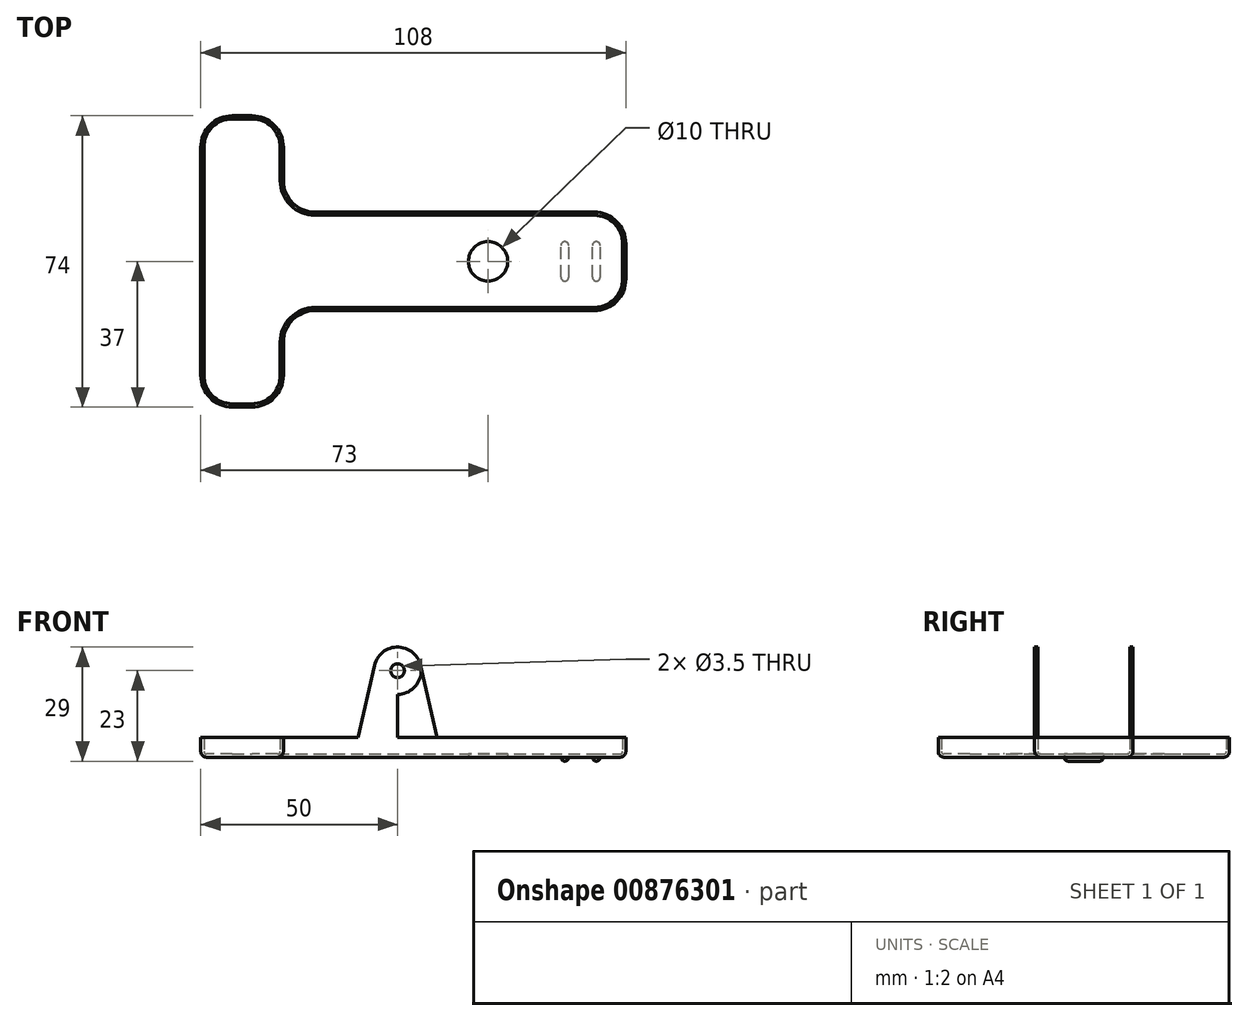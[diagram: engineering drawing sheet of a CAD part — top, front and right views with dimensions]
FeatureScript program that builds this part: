
annotation { "Feature Type Name" : "Feature", "Feature Type Description" : "" }
export const myFeature = defineFeature(function(context is Context, id is Id, definition is map)
    precondition{}
    {
        {
            var Q0;
            Q0=qCreatedBy(makeId("Top.planeOp"),FACE);
            var sketch = newSketch(context, id + "F0", { "sketchPlane" : qUnion([Q0])});
            skLineSegment(sketch, "E0.bottom", {"start": v(54, 12.5) * mm, "end": v(-54, 12.5) * mm});
            skLineSegment(sketch, "E0.top", {"start": v(54, -12.5) * mm, "end": v(-54, -12.5) * mm});
            skLineSegment(sketch, "E0.left", {"start": v(54, 12.5) * mm, "end": v(54, -12.5) * mm});
            skLineSegment(sketch, "E0.right", {"start": v(-54, 12.5) * mm, "end": v(-54, -12.5) * mm});
            skPoint(sketch, "E0.middle", {"position": v(0, 0) * mm});
            skLineSegment(sketch, "E1.bottom", {"start": v(-33, 37) * mm, "end": v(-54, 37) * mm});
            skLineSegment(sketch, "E1.top", {"start": v(-33, -37) * mm, "end": v(-54, -37) * mm});
            skLineSegment(sketch, "E1.left", {"start": v(-33, 37) * mm, "end": v(-33, -37) * mm});
            skLineSegment(sketch, "E1.right", {"start": v(-54, 37) * mm, "end": v(-54, -37) * mm});
            skPoint(sketch, "E1.middle", {"position": v(-43.5, 0) * mm});
            skLineSegment(sketch, "E2", {"start": v(54, 0) * mm, "end": v(19, 0) * mm});
            skCircle(sketch, "E3", {"center": v(19, 0) * mm, "radius": 5 * mm});
            skSolve(sketch);
        }
        {
            var Q0;
            {var subQ5=sQuery(id+"F0.wireOp",EDGE,"E1.top");Q0=makeQuery(id+"F0.imprint","IMPRINT",FACE,{"disambiguationData":[TD([[makeQuery(id+"F0.imprint","IMPRINT",EDGE,{"derivedFrom":subQ5}),-1.0]])]});}
            var Q1;
            {var subQ0=sQuery(id+"F0.wireOp",EDGE,"E1.right");var subQ1=sQuery(id+"F0.wireOp",EDGE,"E0.bottom");var subQ2=makeQuery(id+"F0.imprint","INTERSECT",VERTEX,{"derivedFrom":[subQ1,subQ0]});Q1=makeQuery(id+"F0.imprint","IMPRINT",FACE,{"disambiguationData":[TD([[makeQuery(id+"F0.imprint","IMPRINT",EDGE,{"disambiguationData":[TD([[subQ2,1.0]])],"derivedFrom":subQ1}),1.0]])]});}
            var Q2;
            {var subQ5=sQuery(id+"F0.wireOp",EDGE,"E1.bottom");Q2=makeQuery(id+"F0.imprint","IMPRINT",FACE,{"disambiguationData":[TD([[makeQuery(id+"F0.imprint","IMPRINT",EDGE,{"derivedFrom":subQ5}),1.0]])]});}
            var Q3;
            {var subQ0=sQuery(id+"F0.wireOp",EDGE,"E0.left");Q3=makeQuery(id+"F0.imprint","IMPRINT",FACE,{"disambiguationData":[TD([[makeQuery(id+"F0.imprint","IMPRINT",EDGE,{"derivedFrom":subQ0}),-1.0]])]});}
            var Q4;
            Q4=makeQuery(id+"F0.imprint","IMPRINT",FACE,{"disambiguationData":[TD([[makeQuery(id+"F0.imprint","IMPRINT",EDGE,{"derivedFrom":sQuery(id+"F0.wireOp",EDGE,"E3")}),1.0]])]});
            extrude(context, id + "F1", {"entities" : qUnion([Q0, Q1, Q2, Q3, Q4]), "depth" : 5 * mm, "offsetDistance" : 25 * mm});
        }
        {
            var Q0;
            Q0=makeQuery(id+"F1.opExtrude","SWEPT_EDGE",EDGE,{"disambiguationData":[OSD([sQuery(id+"F0.wireOp",EDGE,"E1.top"),sQuery(id+"F0.wireOp",EDGE,"E1.right")])]});
            var Q1;
            Q1=makeQuery(id+"F1.opExtrude","SWEPT_EDGE",EDGE,{"disambiguationData":[OSD([sQuery(id+"F0.wireOp",EDGE,"E1.top"),sQuery(id+"F0.wireOp",EDGE,"E1.left")])]});
            var Q2;
            Q2=makeQuery(id+"F1.opExtrude","SWEPT_EDGE",EDGE,{"disambiguationData":[OSD([sQuery(id+"F0.wireOp",EDGE,"E0.top"),sQuery(id+"F0.wireOp",EDGE,"E1.left")])]});
            var Q3;
            Q3=makeQuery(id+"F1.opExtrude","SWEPT_EDGE",EDGE,{"disambiguationData":[OSD([sQuery(id+"F0.wireOp",EDGE,"E0.bottom"),sQuery(id+"F0.wireOp",EDGE,"E0.left")])]});
            var Q4;
            Q4=makeQuery(id+"F1.opExtrude","SWEPT_EDGE",EDGE,{"disambiguationData":[OSD([sQuery(id+"F0.wireOp",EDGE,"E0.top"),sQuery(id+"F0.wireOp",EDGE,"E0.left")])]});
            var Q5;
            Q5=makeQuery(id+"F1.opExtrude","SWEPT_EDGE",EDGE,{"disambiguationData":[OSD([sQuery(id+"F0.wireOp",EDGE,"E1.bottom"),sQuery(id+"F0.wireOp",EDGE,"E1.left")])]});
            var Q6;
            Q6=makeQuery(id+"F1.opExtrude","SWEPT_EDGE",EDGE,{"disambiguationData":[OSD([sQuery(id+"F0.wireOp",EDGE,"E1.bottom"),sQuery(id+"F0.wireOp",EDGE,"E1.right")])]});
            var Q7;
            Q7=makeQuery(id+"F1.opExtrude","SWEPT_EDGE",EDGE,{"disambiguationData":[OSD([sQuery(id+"F0.wireOp",EDGE,"E0.bottom"),sQuery(id+"F0.wireOp",EDGE,"E1.left")])]});
            fillet(context, id + "F2", {"entities" : qUnion([Q0, Q1, Q2, Q3, Q4, Q5, Q6, Q7]), "radius" : 8 * mm, "tangentPropagation" : true, "allowEdgeOverflow" : false});
        }
        {
            var Q0;
            Q0=makeQuery(id+"F1.opExtrude","CAP_FACE",FACE,{"disambiguationData":[OSD([sQuery(id+"F0.wireOp",EDGE,"E0.bottom"),sQuery(id+"F0.wireOp",EDGE,"E0.top"),sQuery(id+"F0.wireOp",EDGE,"E0.left"),sQuery(id+"F0.wireOp",EDGE,"E1.bottom"),sQuery(id+"F0.wireOp",EDGE,"E1.top"),sQuery(id+"F0.wireOp",EDGE,"E1.left"),sQuery(id+"F0.wireOp",EDGE,"E1.right")])],"isStart":true});
            fillet(context, id + "F3", {"entities" : qUnion([Q0]), "radius" : 1.5 * mm, "tangentPropagation" : true, "allowEdgeOverflow" : false});
        }
        {
            var Q0;
            Q0=makeQuery(id+"F1.opExtrude","CAP_FACE",FACE,{"disambiguationData":[OSD([sQuery(id+"F0.wireOp",EDGE,"E0.bottom"),sQuery(id+"F0.wireOp",EDGE,"E0.top"),sQuery(id+"F0.wireOp",EDGE,"E0.left"),sQuery(id+"F0.wireOp",EDGE,"E1.bottom"),sQuery(id+"F0.wireOp",EDGE,"E1.top"),sQuery(id+"F0.wireOp",EDGE,"E1.left"),sQuery(id+"F0.wireOp",EDGE,"E1.right")])],"isStart":false});
            shell(context, id + "F4", {"entities" : qUnion([Q0]), "thickness" : 0.8 * mm});
        }
        {
            var Q0;
            Q0=makeQuery(id+"F0.imprint","IMPRINT",FACE,{"disambiguationData":[TD([[makeQuery(id+"F0.imprint","IMPRINT",EDGE,{"derivedFrom":sQuery(id+"F0.wireOp",EDGE,"E3")}),1.0]])]});
            extrude(context, id + "F5", {"entities" : qUnion([Q0]), "operationType" : NewBodyOperationType.REMOVE, "endBound" : BoundingType.SYMMETRIC, "depth" : 3 * mm, "offsetDistance" : 25 * mm});
        }
        {
            var Q0;
            Q0=makeQuery(id+"F1.opExtrude","SWEPT_FACE",FACE,{"disambiguationData":[OSD([sQuery(id+"F0.wireOp",EDGE,"E0.top")])]});
            var sketch = newSketch(context, id + "F6", { "sketchPlane" : qUnion([Q0])});
            skLineSegment(sketch, "E4", {"start": v(46, 5) * mm, "end": v(-4, 5) * mm});
            skLineSegment(sketch, "E5", {"start": v(-4, 5) * mm, "end": v(-4, 22) * mm});
            skCircle(sketch, "E6", {"center": v(-4, 22) * mm, "radius": 1.75 * mm});
            skLineSegment(sketch, "E7", {"start": v(-4, 5) * mm, "end": v(6, 5) * mm});
            skCircle(sketch, "E8", {"center": v(-4, 22) * mm, "radius": 6 * mm});
            skLineSegment(sketch, "E9", {"start": v(6, 5) * mm, "end": v(1.85, 23.32) * mm});
            skLineSegment(sketch, "E10", {"start": v(-4, 5) * mm, "end": v(-14, 5) * mm});
            skLineSegment(sketch, "E11", {"start": v(-14, 5) * mm, "end": v(-9.85, 23.32) * mm});
            skSolve(sketch);
        }
        {
            var Q0;
            Q0=makeQuery(id+"F6.imprint","IMPRINT",FACE,{"disambiguationData":[TD([[makeQuery(id+"F6.imprint","IMPRINT",EDGE,{"derivedFrom":sQuery(id+"F6.wireOp",EDGE,"E6")}),-1.0]])]});
            var Q1;
            {var subQ0=sQuery(id+"F6.wireOp",EDGE,"E10");Q1=makeQuery(id+"F6.imprint","IMPRINT",FACE,{"disambiguationData":[TD([[makeQuery(id+"F6.imprint","IMPRINT",EDGE,{"derivedFrom":subQ0}),-1.0]])]});}
            var Q2;
            {var subQ0=sQuery(id+"F6.wireOp",EDGE,"E7");Q2=makeQuery(id+"F6.imprint","IMPRINT",FACE,{"disambiguationData":[TD([[makeQuery(id+"F6.imprint","IMPRINT",EDGE,{"derivedFrom":subQ0}),-1.0]])]});}
            extrude(context, id + "F7", {"entities" : qUnion([Q0, Q1, Q2]), "operationType" : NewBodyOperationType.ADD, "oppositeDirection" : true, "depth" : 0.8 * mm, "offsetDistance" : 25 * mm});
        }
        {
            var Q0;
            Q0=makeQuery(id+"F1.opExtrude","SWEPT_FACE",FACE,{"disambiguationData":[OSD([sQuery(id+"F0.wireOp",EDGE,"E0.bottom")])]});
            var sketch = newSketch(context, id + "F8", { "sketchPlane" : qUnion([Q0])});
            skLineSegment(sketch, "E12", {"start": v(4, 5) * mm, "end": v(4, 22) * mm});
            skCircle(sketch, "E13", {"center": v(4, 22) * mm, "radius": 1.75 * mm});
            skLineSegment(sketch, "E14", {"start": v(4, 5) * mm, "end": v(14, 5) * mm});
            skCircle(sketch, "E15", {"center": v(4, 22) * mm, "radius": 6 * mm});
            skLineSegment(sketch, "E16", {"start": v(14, 5) * mm, "end": v(9.85, 23.32) * mm});
            skLineSegment(sketch, "E17", {"start": v(4, 5) * mm, "end": v(-6, 5) * mm});
            skLineSegment(sketch, "E18", {"start": v(-6, 5) * mm, "end": v(-1.85, 23.32) * mm});
            skLineSegment(sketch, "E19", {"start": v(-46, 5) * mm, "end": v(4, 5) * mm});
            skSolve(sketch);
        }
        {
            var Q0;
            Q0=makeQuery(id+"F8.imprint","IMPRINT",FACE,{"disambiguationData":[TD([[makeQuery(id+"F8.imprint","IMPRINT",EDGE,{"derivedFrom":sQuery(id+"F8.wireOp",EDGE,"E13")}),-1.0]])]});
            var Q1;
            {var subQ0=sQuery(id+"F8.wireOp",EDGE,"E14");Q1=makeQuery(id+"F8.imprint","IMPRINT",FACE,{"disambiguationData":[TD([[makeQuery(id+"F8.imprint","IMPRINT",EDGE,{"derivedFrom":subQ0}),1.0]])]});}
            var Q2;
            {var subQ5=sQuery(id+"F8.wireOp",EDGE,"E18");Q2=makeQuery(id+"F8.imprint","IMPRINT",FACE,{"disambiguationData":[TD([[makeQuery(id+"F8.imprint","IMPRINT",EDGE,{"derivedFrom":subQ5}),-1.0]])]});}
            extrude(context, id + "F9", {"entities" : qUnion([Q0, Q1, Q2]), "operationType" : NewBodyOperationType.ADD, "oppositeDirection" : true, "depth" : 0.8 * mm, "offsetDistance" : 25 * mm});
        }
        {
            var Q0;
            Q0=qCreatedBy(makeId("Front.planeOp"),FACE);
            var sketch = newSketch(context, id + "F10", { "sketchPlane" : qUnion([Q0])});
            skLineSegment(sketch, "E20", {"start": v(52.5, 0) * mm, "end": v(46.5, 0) * mm});
            skLineSegment(sketch, "E21", {"start": v(46.5, 0) * mm, "end": v(38.5, 0) * mm});
            skCircle(sketch, "E22", {"center": v(46.5, 0) * mm, "radius": 1 * mm});
            skCircle(sketch, "E23", {"center": v(38.5, 0) * mm, "radius": 1 * mm});
            skLineSegment(sketch, "E24", {"start": v(38.5, 0) * mm, "end": v(37.5, 0) * mm});
            skSolve(sketch);
        }
        {
            var Q0;
            {var subQ0=sQuery(id+"F10.wireOp",EDGE,"E24");Q0=makeQuery(id+"F10.imprint","IMPRINT",FACE,{"disambiguationData":[TD([[makeQuery(id+"F10.imprint","IMPRINT",EDGE,{"derivedFrom":subQ0}),1.0]])]});}
            var Q1;
            {var subQ0=sQuery(id+"F10.wireOp",EDGE,"E21");var subQ1=sQuery(id+"F10.wireOp",EDGE,"E20");var subQ2=makeQuery(id+"F10.imprint","INTERSECT",VERTEX,{"derivedFrom":[subQ1,subQ0]});Q1=makeQuery(id+"F10.imprint","IMPRINT",FACE,{"disambiguationData":[TD([[makeQuery(id+"F10.imprint","IMPRINT",EDGE,{"disambiguationData":[TD([[subQ2,1.0]])],"derivedFrom":subQ1}),1.0]])]});}
            extrude(context, id + "F11", {"entities" : qUnion([Q0, Q1]), "operationType" : NewBodyOperationType.ADD, "endBound" : BoundingType.SYMMETRIC, "depth" : 10 * mm, "offsetDistance" : 25 * mm});
        }
        {
            var Q0;
            Q0=makeQuery(id+"F11.opExtrude","CAP_EDGE",EDGE,{"disambiguationData":[OSD([sQuery(id+"F10.wireOp",EDGE,"E22")])],"isStart":false});
            var Q1;
            Q1=makeQuery(id+"F11.opExtrude","CAP_EDGE",EDGE,{"disambiguationData":[OSD([sQuery(id+"F10.wireOp",EDGE,"E23")])],"isStart":false});
            var Q2;
            Q2=makeQuery(id+"F11.opExtrude","CAP_EDGE",EDGE,{"disambiguationData":[OSD([sQuery(id+"F10.wireOp",EDGE,"E22")])],"isStart":true});
            var Q3;
            Q3=makeQuery(id+"F11.opExtrude","CAP_EDGE",EDGE,{"disambiguationData":[OSD([sQuery(id+"F10.wireOp",EDGE,"E23")])],"isStart":true});
            fillet(context, id + "F12", {"entities" : qUnion([Q0, Q1, Q2, Q3]), "radius" : 1 * mm, "tangentPropagation" : true, "allowEdgeOverflow" : false});
        }
    });
